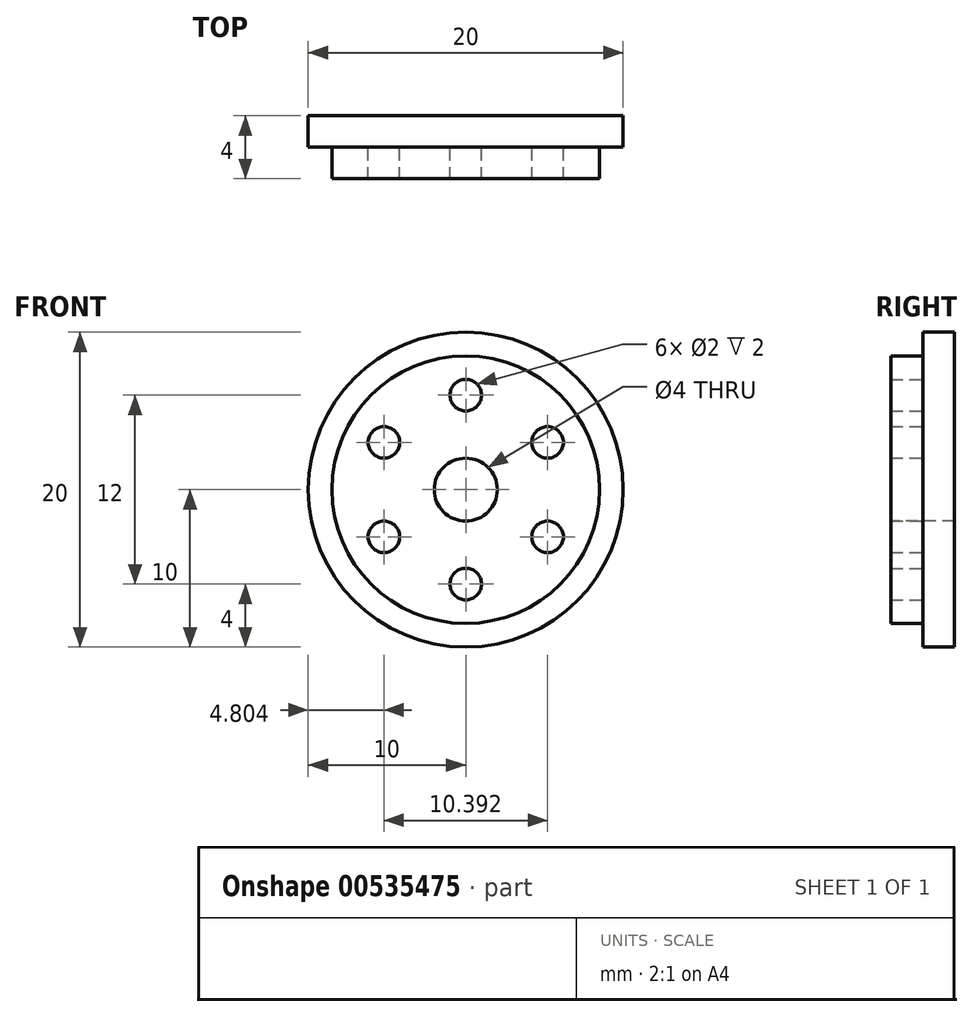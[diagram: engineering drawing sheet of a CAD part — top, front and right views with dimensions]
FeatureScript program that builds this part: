
annotation { "Feature Type Name" : "Feature", "Feature Type Description" : "" }
export const myFeature = defineFeature(function(context is Context, id is Id, definition is map)
    precondition{}
    {
        {
            var Q0;
            Q0=qCreatedBy(makeId("Front.planeOp"),FACE);
            var sketch = newSketch(context, id + "F0", { "sketchPlane" : qUnion([Q0])});
            skCircle(sketch, "E0", {"center": v(0, 0) * mm, "radius": 8.5 * mm});
            skCircle(sketch, "E1", {"center": v(0, 0) * mm, "radius": 6 * mm, "construction": true});
            skCircle(sketch, "E2", {"center": v(0, 6) * mm, "radius": 1 * mm});
            skCircle(sketch, "E3.1.0", {"center": v(-5.2, 3) * mm, "radius": 1 * mm});
            skCircle(sketch, "E3.2.0", {"center": v(-5.2, -3) * mm, "radius": 1 * mm});
            skCircle(sketch, "E3.3.0", {"center": v(0, -6) * mm, "radius": 1 * mm});
            skCircle(sketch, "E3.4.0", {"center": v(5.2, -3) * mm, "radius": 1 * mm});
            skCircle(sketch, "E3.5.0", {"center": v(5.2, 3) * mm, "radius": 1 * mm});
            skSolve(sketch);
        }
        {
            var Q0;
            Q0 = qSketchRegion(id + "F0", true);
            extrude(context, id + "F1", {"entities" : qUnion([Q0]), "depth" : 2 * mm, "offsetDistance" : 25 * mm});
        }
        {
            var Q0;
            Q0=makeQuery(id+"F1.opExtrude","CAP_FACE",FACE,{"disambiguationData":[OSD([sQuery(id+"F0.wireOp",EDGE,"E0")])],"isStart":true});
            var sketch = newSketch(context, id + "F2", { "sketchPlane" : qUnion([Q0])});
            skCircle(sketch, "E4", {"center": v(0, 0) * mm, "radius": 10 * mm});
            skSolve(sketch);
        }
        {
            var Q0;
            Q0 = qSketchRegion(id + "F2", true);
            extrude(context, id + "F3", {"entities" : qUnion([Q0]), "operationType" : NewBodyOperationType.ADD, "depth" : 2 * mm, "offsetDistance" : 25 * mm});
        }
        {
            var Q0;
            Q0=makeQuery(id+"F1.opExtrude","CAP_FACE",FACE,{"disambiguationData":[OSD([sQuery(id+"F0.wireOp",EDGE,"E0")])],"isStart":false});
            var sketch = newSketch(context, id + "F4", { "sketchPlane" : qUnion([Q0])});
            skCircle(sketch, "E5", {"center": v(0, 0) * mm, "radius": 2 * mm});
            skSolve(sketch);
        }
        {
            var Q0;
            Q0 = qSketchRegion(id + "F4", true);
            extrude(context, id + "F5", {"entities" : qUnion([Q0]), "operationType" : NewBodyOperationType.REMOVE, "endBound" : BoundingType.THROUGH_ALL, "oppositeDirection" : true, "depth" : 25 * mm, "offsetDistance" : 25 * mm});
        }
    });
